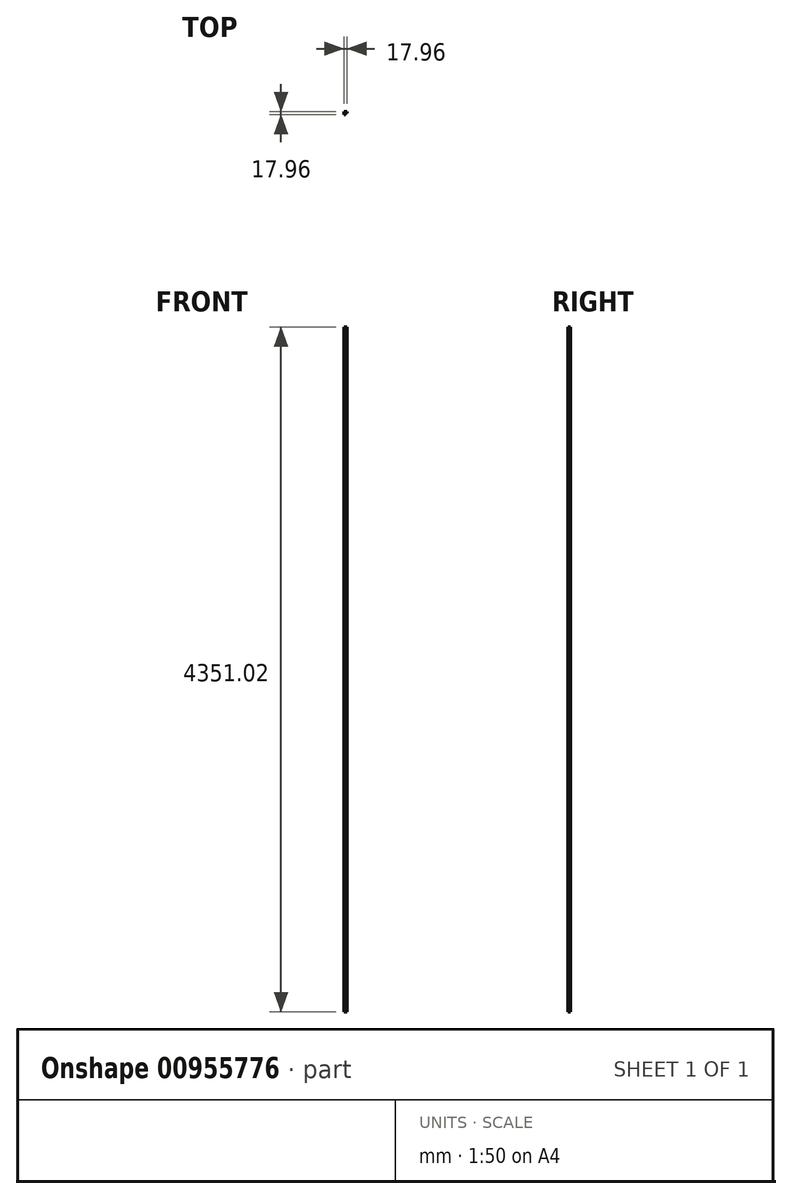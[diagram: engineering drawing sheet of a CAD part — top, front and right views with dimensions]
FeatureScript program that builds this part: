
annotation { "Feature Type Name" : "Feature", "Feature Type Description" : "" }
export const myFeature = defineFeature(function(context is Context, id is Id, definition is map)
    precondition{}
    {
        {
            var Q0;
            Q0=qCreatedBy(makeId("Top.planeOp"),FACE);
            var sketch = newSketch(context, id + "F0", { "sketchPlane" : qUnion([Q0])});
            skLineSegment(sketch, "E0.bottom", {"start": v(-43.45, -9.68) * mm, "end": v(-61.4, -9.68) * mm});
            skLineSegment(sketch, "E0.top", {"start": v(-43.45, 8.28) * mm, "end": v(-61.4, 8.28) * mm});
            skLineSegment(sketch, "E0.left", {"start": v(-43.45, -9.68) * mm, "end": v(-43.45, 8.28) * mm});
            skLineSegment(sketch, "E0.right", {"start": v(-61.4, -9.68) * mm, "end": v(-61.4, 8.28) * mm});
            skPoint(sketch, "E0.middle", {"position": v(-52.43, -0.7) * mm});
            skLineSegment(sketch, "E1", {"start": v(-52.43, -0.7) * mm, "end": v(-43.45, -0.7) * mm});
            skCircle(sketch, "E2", {"center": v(-43.45, -9.68) * mm, "radius": 8.98 * mm});
            skSolve(sketch);
        }
        {
            var Q0;
            {var subQ2=sQuery(id+"F0.wireOp",EDGE,"E0.top");Q0=makeQuery(id+"F0.imprint","IMPRINT",FACE,{"disambiguationData":[TD([[makeQuery(id+"F0.imprint","IMPRINT",EDGE,{"derivedFrom":subQ2}),1.0]])]});}
            extrude(context, id + "F1", {"entities" : qUnion([Q0]), "depth" : 4351.02 * mm, "offsetDistance" : 25.4 * mm});
        }
    });
